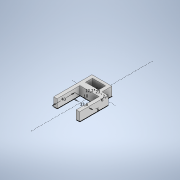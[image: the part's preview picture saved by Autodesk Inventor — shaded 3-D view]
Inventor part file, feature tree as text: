
AUTODESK INVENTOR PART (.ipt)
format: ipt  version: 2020.3 (Build 243373000, 373)  size: 118,784 bytes
history: native  units: mm
features: extrude x1, sketch x1
ambient origin geometry x8: Origin, YZ Plane, XZ Plane, XY Plane, X Axis, Y Axis, Z Axis, Center Point
bodies: Solid1 (feature_tree)
feature tree (2):
  extrude  "Extrusion1"  Depth=12.2mm
  sketch  "Sketch1"  dims[d4=23.0mm d5=12.2mm d8=2.7mm d9=5.0mm d11=10.0mm d12=40.0mm d14=33.6mm d15=6.0mm d16=6.0mm d17=15.0mm d18=0.0mm]
